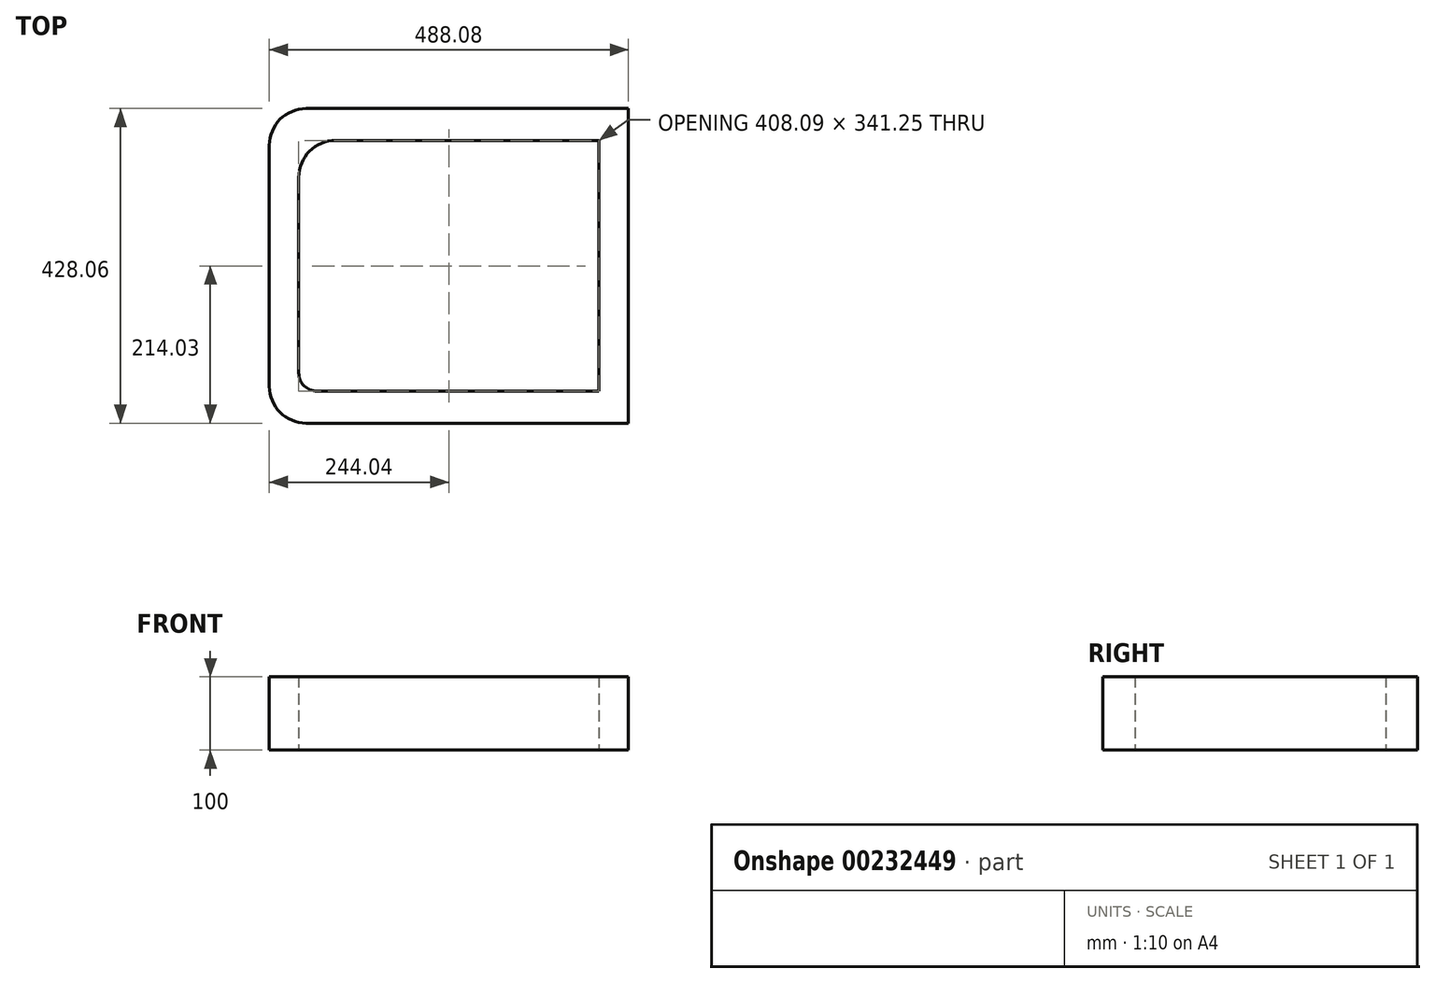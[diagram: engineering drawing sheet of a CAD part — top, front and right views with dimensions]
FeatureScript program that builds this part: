
annotation { "Feature Type Name" : "Feature", "Feature Type Description" : "" }
export const myFeature = defineFeature(function(context is Context, id is Id, definition is map)
    precondition{}
    {
        {
            var Q0;
            Q0=qCreatedBy(makeId("Top.planeOp"),FACE);
            var sketch = newSketch(context, id + "F0", { "sketchPlane" : qUnion([Q0])});
            skLineSegment(sketch, "E0.bottom", {"start": v(-244.04, 214.03) * mm, "end": v(244.04, 214.03) * mm});
            skLineSegment(sketch, "E0.top", {"start": v(-244.04, -214.03) * mm, "end": v(244.04, -214.03) * mm});
            skLineSegment(sketch, "E0.left", {"start": v(-244.04, 214.03) * mm, "end": v(-244.04, -214.03) * mm});
            skLineSegment(sketch, "E0.right", {"start": v(244.04, 214.03) * mm, "end": v(244.04, -214.03) * mm});
            skPoint(sketch, "E0.middle", {"position": v(0, 0) * mm});
            skLineSegment(sketch, "E1.bottom", {"start": v(-204.04, 170.63) * mm, "end": v(204.04, 170.63) * mm});
            skLineSegment(sketch, "E1.top", {"start": v(-204.04, -170.63) * mm, "end": v(204.04, -170.63) * mm});
            skLineSegment(sketch, "E1.left", {"start": v(-204.04, 170.63) * mm, "end": v(-204.04, -170.63) * mm});
            skLineSegment(sketch, "E1.right", {"start": v(204.04, 170.63) * mm, "end": v(204.04, -170.63) * mm});
            skSolve(sketch);
        }
        {
            var Q0;
            Q0=makeQuery(id+"F0.imprint","IMPRINT",FACE,{"disambiguationData":[TD([[makeQuery(id+"F0.imprint","IMPRINT",EDGE,{"derivedFrom":sQuery(id+"F0.wireOp",EDGE,"E0.bottom")}),-1.0]])]});
            extrude(context, id + "F1", {"entities" : qUnion([Q0]), "depth" : 100 * mm});
        }
        {
            var Q0;
            Q0=makeQuery(id+"F1.opExtrude","SWEPT_EDGE",EDGE,{"disambiguationData":[OSD([sQuery(id+"F0.wireOp",EDGE,"E0.bottom"),sQuery(id+"F0.wireOp",EDGE,"E0.left")])]});
            var Q1;
            Q1=makeQuery(id+"F1.opExtrude","SWEPT_EDGE",EDGE,{"disambiguationData":[OSD([sQuery(id+"F0.wireOp",EDGE,"E0.top"),sQuery(id+"F0.wireOp",EDGE,"E0.left")])]});
            var Q2;
            Q2=makeQuery(id+"F1.opExtrude","SWEPT_EDGE",EDGE,{"disambiguationData":[OSD([sQuery(id+"F0.wireOp",EDGE,"E1.bottom"),sQuery(id+"F0.wireOp",EDGE,"E1.left")])]});
            fillet(context, id + "F2", {"entities" : qUnion([Q0, Q1, Q2]), "radius" : 50 * mm, "tangentPropagation" : true, "allowEdgeOverflow" : false});
        }
        {
            var Q0;
            Q0=makeQuery(id+"F1.opExtrude","SWEPT_EDGE",EDGE,{"disambiguationData":[OSD([sQuery(id+"F0.wireOp",EDGE,"E1.top"),sQuery(id+"F0.wireOp",EDGE,"E1.left")])]});
            fillet(context, id + "F3", {"entities" : qUnion([Q0]), "radius" : 25 * mm, "tangentPropagation" : true, "allowEdgeOverflow" : false});
        }
    });
